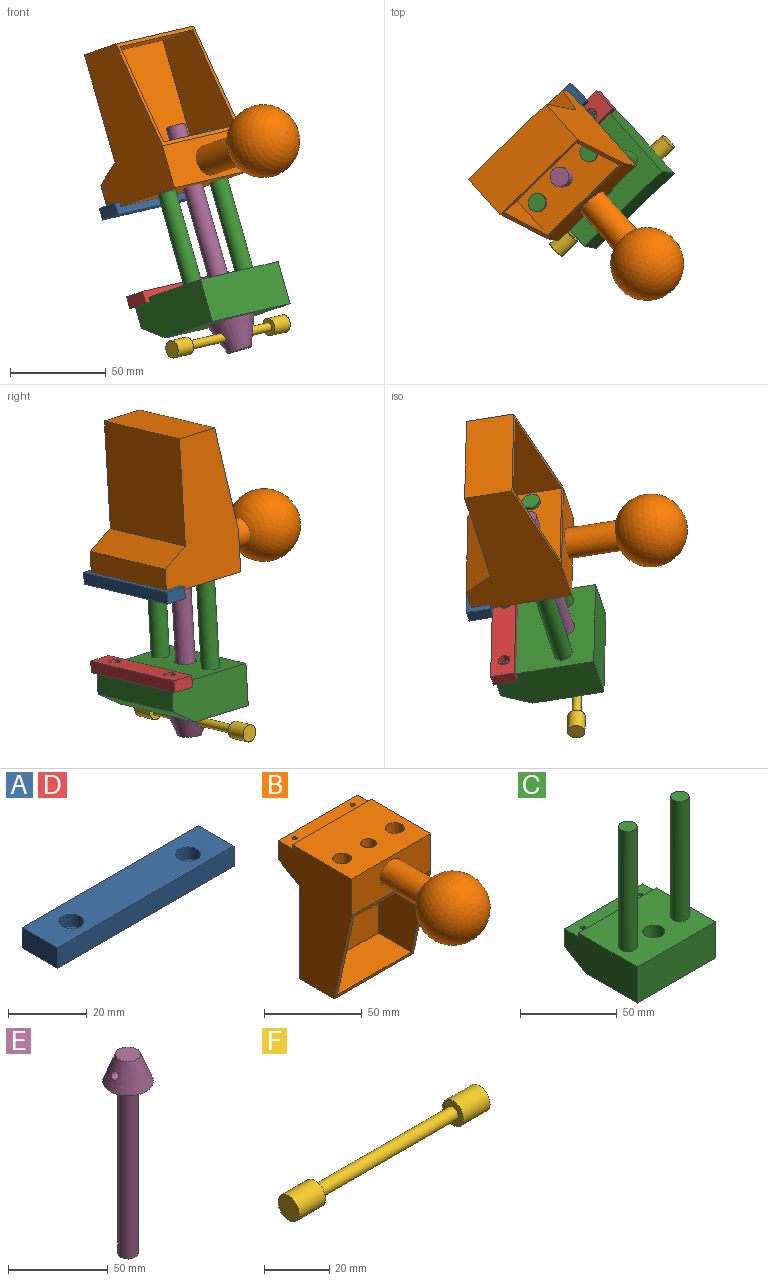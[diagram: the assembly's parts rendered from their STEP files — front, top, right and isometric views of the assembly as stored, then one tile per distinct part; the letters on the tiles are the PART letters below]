
ASSEMBLY  parts=6 mates=10
PART A: 12 faces, bbox 63.5x12.7x6.4 mm
  f0: plane 12.7x6.35mm, normal (1,0,0), area 80.6mm2, adj f1,f3,f4,f5
  f1: plane 63.5x6.35mm, normal (0,1,0), area 403.2mm2, adj f0,f2,f4,f5
  f2: plane 12.7x6.35mm, normal (-1,0,0), area 80.6mm2, adj f1,f3,f4,f5
  f3: plane 63.5x6.35mm, normal (0,-1,0), area 403.2mm2, adj f0,f2,f4,f5
  f4: plane 63.5x12.7mm, normal (0,0,1), area 743.1mm2, adj f0,f1,f2,f3,f8,f11
  f5: plane 63.5x12.7mm, normal (0,0,-1), area 780.5mm2, adj f0,f1,f2,f3,f6,f9
  f6: cylinder r=2.03mm len=4.06mm, axis (0,0,1), area 32.4mm2, adj f5,f7
  f7: plane 6.35x6.35mm, normal (0,0,1), area 18.7mm2, adj f6,f8
  f8: cylinder r=3.17mm len=6.35mm, axis (0,0,1), area 76mm2, adj f4,f7
  f9: cylinder r=2.03mm len=4.06mm, axis (0,0,1), area 32.4mm2, adj f5,f10
  f10: plane 6.35x6.35mm, normal (0,0,1), area 18.7mm2, adj f9,f11
  f11: cylinder r=3.17mm len=6.35mm, axis (0,0,1), area 76mm2, adj f4,f10
PART B: 25 faces, bbox 57.2x116.8x90.2 mm
  f0: plane 57.15x43.18mm, normal (0,0,1), area 2275.7mm2, adj f1,f2,f9,f10,f18,f19,f20
  f1: plane 57.15x2.54mm, normal (0,1,0), area 145.2mm2, adj f0,f8,f9,f10
  f2: plane 57.15x22.86mm, normal (0,-1,0), area 1108.5mm2, adj f0,f3,f9,f10,f12
  f3: plane 58.42x57.15mm, normal (0,-0.98,-0.21), area 435.8mm2, adj f2,f4,f9,f10,f13,f14,f15,f16
  f4: plane 57.15x25.4mm, normal (0,0,-1), area 1451.6mm2, adj f3,f5,f9,f10
  f5: plane 58.42x57.15mm, normal (0,1,0), area 3338.7mm2, adj f4,f6,f9,f10
  f6: plane 57.15x15.24mm, normal (0,0.5,-0.86), area 1008.3mm2, adj f5,f7,f9,f10
  f7: plane 57.15x11.43mm, normal (0,1,0), area 653.2mm2, adj f6,f8,f9,f10
  f8: plane 57.15x10.16mm, normal (0,0,1), area 570.2mm2, adj f1,f7,f9,f10,f22,f24
  f9: plane 81.28x53.34mm, normal (1,0,0), area 2980.6mm2, adj f0,f1,f2,f3,f4,f5,f6,f7
  f10: plane 81.28x53.34mm, normal (-1,0,0), area 2980.6mm2, adj f0,f1,f2,f3,f4,f5,f6,f7
  f11: sphere r=19.05mm, area 4353mm2, adj f12
  f12: cylinder r=7.94mm len=27.13mm, axis (0,1,0), area 1353.2mm2, adj f2,f11
  f13: plane 53.34x23.91mm, normal (0,0,1), area 1275.3mm2, adj f3,f14,f16,f17
  f14: plane 54.61x35.78mm, normal (-1,0,0), area 1629.8mm2, adj f3,f13,f15,f17
  f15: plane 53.34x35.78mm, normal (0,0,-1), area 1716.6mm2, adj f3,f14,f16,f17,f18,f19,f20
  f16: plane 54.61x35.78mm, normal (1,0,0), area 1629.8mm2, adj f3,f13,f15,f17
  f17: plane 54.61x53.34mm, normal (0,-1,0), area 2912.9mm2, adj f13,f14,f15,f16
  f18: cylinder r=4.76mm len=24.77mm, axis (0,0,1), area 741.1mm2, adj f0,f15
  f19: cylinder r=4.76mm len=24.77mm, axis (0,0,1), area 741.1mm2, adj f0,f15
  f20: cylinder r=3.97mm len=24.77mm, axis (0,0,1), area 617.5mm2, adj f0,f15
  f21: cone r=1.29mm half-angle=59deg, axis (0,0,1), area 6.1mm2, adj f22
  f22: cylinder r=1.29mm len=5.08mm, axis (0,0,1), area 41.1mm2, adj f8,f21
  f23: cone r=1.29mm half-angle=59deg, axis (0,0,1), area 6.1mm2, adj f24
  f24: cylinder r=1.29mm len=5.08mm, axis (0,0,1), area 41.1mm2, adj f8,f23
PART C: 18 faces, bbox 57.2x53.3x99.1 mm
  f0: plane 57.15x43.18mm, normal (0,0,1), area 2222.6mm2, adj f1,f6,f7,f8,f13,f14,f16
  f1: plane 57.15x22.86mm, normal (0,-1,0), area 1306.4mm2, adj f0,f2,f7,f8
  f2: plane 57.15x38.1mm, normal (0,0,-1), area 2074.8mm2, adj f1,f3,f7,f8,f13
  f3: plane 57.15x15.24mm, normal (0,0.5,-0.86), area 1008.3mm2, adj f2,f4,f7,f8
  f4: plane 57.15x11.43mm, normal (0,1,0), area 653.2mm2, adj f3,f5,f7,f8
  f5: plane 57.15x10.16mm, normal (0,0,1), area 570.2mm2, adj f4,f6,f7,f8,f10,f12
  f6: plane 57.15x2.54mm, normal (0,1,0), area 145.2mm2, adj f0,f5,f7,f8
  f7: plane 53.34x22.86mm, normal (1,0,0), area 1125.8mm2, adj f0,f1,f2,f3,f4,f5,f6
  f8: plane 53.34x22.86mm, normal (-1,0,0), area 1125.8mm2, adj f0,f1,f2,f3,f4,f5,f6
  f9: cone r=1.29mm half-angle=59deg, axis (0,0,1), area 6.1mm2, adj f10
  f10: cylinder r=1.29mm len=5.08mm, axis (0,0,1), area 41.1mm2, adj f5,f9
  f11: cone r=1.29mm half-angle=59deg, axis (0,0,1), area 6.1mm2, adj f12
  f12: cylinder r=1.29mm len=5.08mm, axis (0,0,1), area 41.1mm2, adj f5,f11
  f13: cylinder r=5.71mm len=22.86mm, axis (0,0,1), area 820.9mm2, adj f0,f2
  f14: cylinder r=4.76mm len=76.2mm, axis (0,0,-1), area 2280.2mm2, adj f0,f15
  f15: plane 9.53x9.53mm, normal (0,0,1), area 71.3mm2, adj f14
  f16: cylinder r=4.76mm len=76.2mm, axis (0,0,-1), area 2280.2mm2, adj f0,f17
  f17: plane 9.53x9.53mm, normal (0,0,1), area 71.3mm2, adj f16
PART D: same geometry as A
PART E: 6 faces, bbox 25.4x25.4x121.9 mm
  f0: cone r=12.7mm half-angle=21deg, axis (0,0,-1), area 1023.2mm2, adj f1,f2,f5
  f1: plane 12.7x12.7mm, normal (0,0,1), area 126.7mm2, adj f0
  f2: plane 25.4x25.4mm, normal (0,0,-1), area 425.6mm2, adj f0,f3
  f3: cylinder r=5.08mm len=105.41mm, axis (0,0,1), area 3364.5mm2, adj f2,f4
  f4: plane 10.16x10.16mm, normal (0,0,-1), area 81.1mm2, adj f3
  f5: cylinder r=2.29mm len=20.81mm, axis (-1,0,0), area 269.6mm2, adj f0
PART F: 7 faces, bbox 82.6x9.1x9.1 mm
  f0: plane 9.14x9.14mm, normal (-1,0,0), area 65.7mm2, adj f1
  f1: cylinder r=4.57mm len=11.43mm, axis (-1,0,0), area 328.3mm2, adj f0,f2
  f2: plane 9.14x9.14mm, normal (1,0,0), area 49.3mm2, adj f1,f3
  f3: cylinder r=2.29mm len=59.69mm, axis (-1,0,0), area 857.3mm2, adj f2,f4
  f4: plane 9.14x9.14mm, normal (-1,0,0), area 49.3mm2, adj f3,f5
  f5: cylinder r=4.57mm len=11.43mm, axis (-1,0,0), area 328.3mm2, adj f4,f6
  f6: plane 9.14x9.14mm, normal (1,0,0), area 65.7mm2, adj f5
PLACE A rot(axis=(-0.2,-0.31,0.93),45.7deg) t=(21.32,55.58,7)mm
PLACE B rot(axis=(-0.36,0.93,-0.08),166.4deg) t=(15.05,14.66,11.49)mm
PLACE C rot(axis=(-0.2,-0.31,0.93),45.7deg) t=(28.66,11.98,-36.3)mm
PLACE D rot(axis=(-0.2,-0.31,0.93),45.7deg) t=(35.56,51.87,-39.23)mm
PLACE E rot(axis=(0.92,0.36,0.12),171.3deg) t=(34.92,10.74,-58.26)mm
PLACE F rot(axis=(-0.2,-0.31,0.93),45.7deg) t=(62.85,35.08,-60.26)mm
MATE cylindrical C.f14 <-> B.f18  axis (0.27,-0.05,-0.96) through (4.72,0.98,-2.83)mm
MATE planar B.f8 <-> A.f4  axis (0.27,-0.05,-0.96) through (-6.25,37.85,6.76)mm
MATE cylindrical F.f1 <-> E.f5  axis (-0.71,-0.69,-0.16) through (33.55,6.8,-67.02)mm
MATE revolute E.f0 <-> C.f13  axis (-0.27,0.05,0.96) through (34.92,10.74,-58.26)mm
MATE cylindrical C.f16 <-> B.f19  axis (0.27,-0.05,-0.96) through (31.76,27.08,3.4)mm
MATE planar D.f5 <-> C.f5  axis (0.27,-0.05,-0.96) through (8.89,34.74,-45.86)mm
MATE cylindrical D.f6 <-> C.f9  axis (0.27,-0.05,-0.96) through (24.19,48.62,-42.28)mm
MATE cylindrical A.f9 <-> B.f21  axis (0.27,-0.05,-0.96) through (-19.8,23.62,-2.91)mm
MATE cylindrical A.f6 <-> B.f23  axis (-0.27,0.05,0.96) through (8.21,52.68,10.05)mm
MATE cylindrical D.f9 <-> C.f11  axis (-0.27,0.05,0.96) through (-7.3,20.25,-43.04)mm
